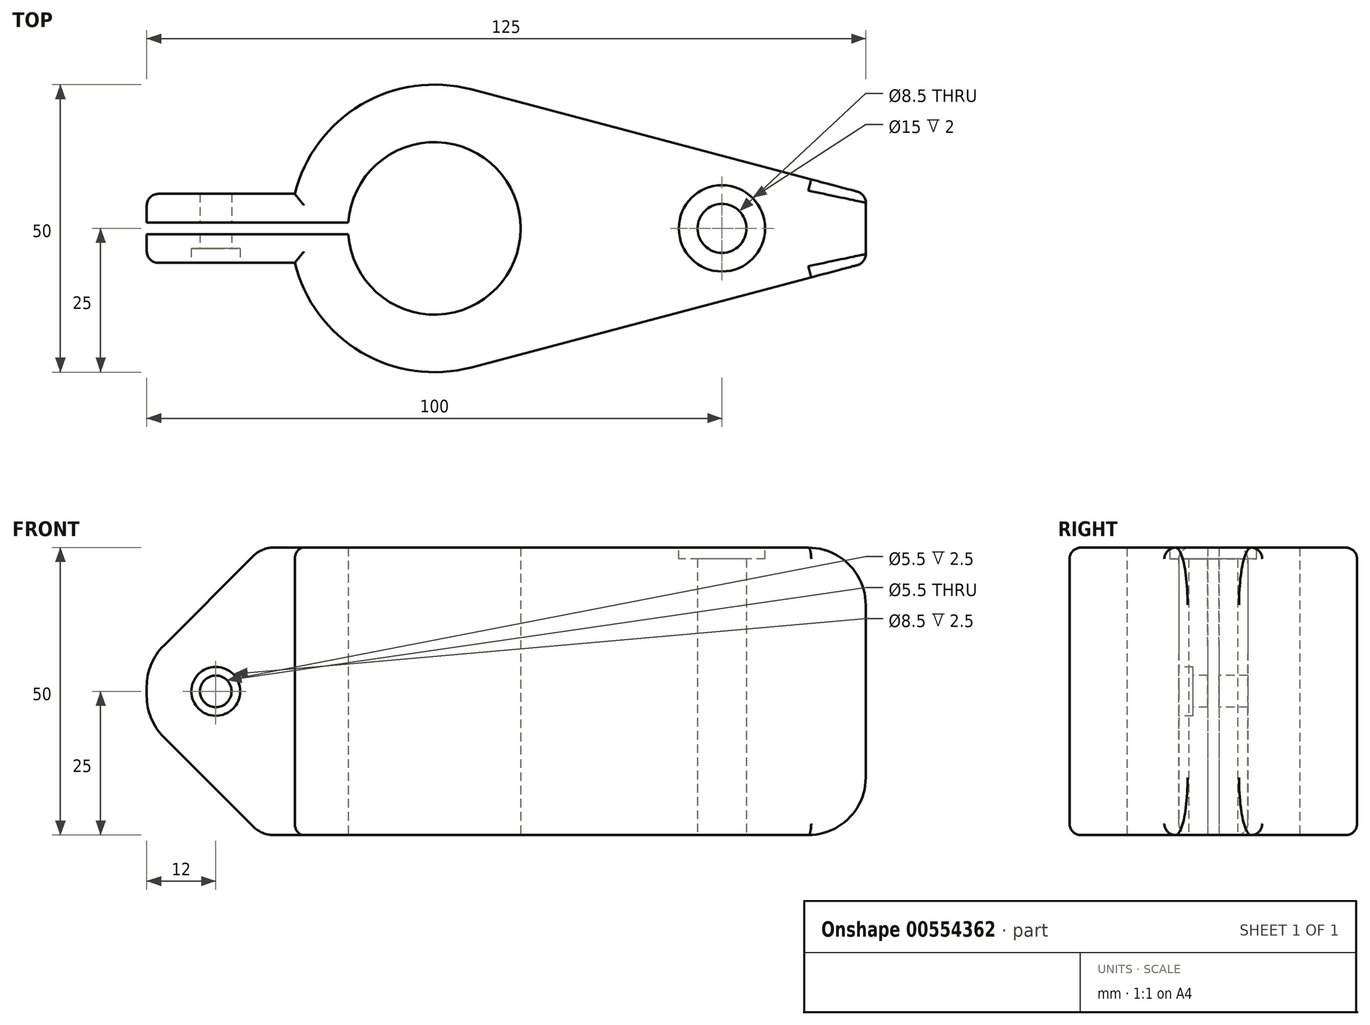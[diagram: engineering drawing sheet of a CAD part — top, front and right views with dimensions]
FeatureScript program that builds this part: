
annotation { "Feature Type Name" : "Feature", "Feature Type Description" : "" }
export const myFeature = defineFeature(function(context is Context, id is Id, definition is map)
    precondition{}
    {
        {
            var Q0;
            Q0=qCreatedBy(makeId("Top.planeOp"),FACE);
            var sketch = newSketch(context, id + "F0", { "sketchPlane" : qUnion([Q0])});
            skArc(sketch, "E0", {"start": v(-14.97, -1) * mm, "mid": v(15, 0) * mm, "end": v(-14.97, 1) * mm});
            skLineSegment(sketch, "E1", {"start": v(0, 0) * mm, "end": v(50, 0) * mm});
            skCircle(sketch, "E2", {"center": v(50, 0) * mm, "radius": 4.25 * mm});
            skLineSegment(sketch, "E3", {"start": v(75, 6) * mm, "end": v(75, 6) * mm});
            skLineSegment(sketch, "E4", {"start": v(75, -6) * mm, "end": v(75, -6) * mm});
            skLineSegment(sketch, "E5", {"start": v(0, 0) * mm, "end": v(75, 0) * mm, "construction": true});
            skLineSegment(sketch, "E6", {"start": v(75, 0) * mm, "end": v(75, 6) * mm, "construction": true});
            skLineSegment(sketch, "E7", {"start": v(75, 6) * mm, "end": v(75, 0) * mm});
            skLineSegment(sketch, "E8", {"start": v(75, -6) * mm, "end": v(75, 0) * mm});
            skArc(sketch, "E9", {"start": v(6.4, 24.17) * mm, "mid": v(-12.74, 21.5) * mm, "end": v(-24.27, 6) * mm});
            skLineSegment(sketch, "E10", {"start": v(75, 6) * mm, "end": v(6.4, 24.17) * mm});
            skLineSegment(sketch, "E11", {"start": v(75, -6) * mm, "end": v(6.4, -24.17) * mm});
            skLineSegment(sketch, "E12", {"start": v(0, 0) * mm, "end": v(0, 1) * mm});
            skLineSegment(sketch, "E13", {"start": v(-14.97, 1) * mm, "end": v(-50, 1) * mm});
            skLineSegment(sketch, "E14.bottom", {"start": v(-50, 6) * mm, "end": v(-24.27, 6) * mm});
            skLineSegment(sketch, "E14.top", {"start": v(-50, -6) * mm, "end": v(-24.27, -6) * mm});
            skLineSegment(sketch, "E15", {"start": v(0, 0) * mm, "end": v(-50, 0) * mm, "construction": true});
            skLineSegment(sketch, "E16", {"start": v(-50, 1) * mm, "end": v(-50, 6) * mm});
            skLineSegment(sketch, "E17", {"start": v(-50, -1) * mm, "end": v(-50, -6) * mm});
            skLineSegment(sketch, "E18", {"start": v(-14.97, -1) * mm, "end": v(-50, -1) * mm});
            skLineSegment(sketch, "E19", {"start": v(0, -1) * mm, "end": v(0, 0) * mm});
            skArc(sketch, "E20.trimOffspring", {"start": v(-24.27, -6) * mm, "mid": v(-12.74, -21.5) * mm, "end": v(6.4, -24.17) * mm});
            skSolve(sketch);
        }
        {
            var Q0;
            Q0=qSketchRegion(id+"F0",true);
            extrude(context, id + "F1", {"entities" : qUnion([Q0]), "depth" : 50 * mm, "offsetDistance" : 25 * mm});
        }
        {
            var Q0;
            Q0=makeQuery(id+"F1.opExtrude","CAP_FACE",FACE,{"disambiguationData":[OSD([sQuery(id+"F0.wireOp",EDGE,"E0"),sQuery(id+"F0.wireOp",EDGE,"E2"),sQuery(id+"F0.wireOp",EDGE,"E3"),sQuery(id+"F0.wireOp",EDGE,"E4"),sQuery(id+"F0.wireOp",EDGE,"E7"),sQuery(id+"F0.wireOp",EDGE,"E8"),sQuery(id+"F0.wireOp",EDGE,"E9"),sQuery(id+"F0.wireOp",EDGE,"E10"),sQuery(id+"F0.wireOp",EDGE,"E11")])],"isStart":false});
            var sketch = newSketch(context, id + "F2", { "sketchPlane" : qUnion([Q0])});
            skCircle(sketch, "E21", {"center": v(50, 0) * mm, "radius": 7.5 * mm});
            skSolve(sketch);
        }
        {
            var Q0;
            Q0=qSketchRegion(id+"F2",true);
            extrude(context, id + "F3", {"entities" : qUnion([Q0]), "operationType" : NewBodyOperationType.REMOVE, "oppositeDirection" : true, "depth" : 2 * mm, "offsetDistance" : 25 * mm});
        }
        {
            var Q0;
            Q0=makeQuery(id+"F1.opExtrude","CAP_EDGE",EDGE,{"disambiguationData":[OSD([sQuery(id+"F0.wireOp",EDGE,"E7"),sQuery(id+"F0.wireOp",EDGE,"E8")])],"isStart":false});
            var Q1;
            Q1=makeQuery(id+"F1.opExtrude","CAP_EDGE",EDGE,{"disambiguationData":[OSD([sQuery(id+"F0.wireOp",EDGE,"E7"),sQuery(id+"F0.wireOp",EDGE,"E8")])],"isStart":true});
            fillet(context, id + "F4", {"entities" : qUnion([Q0, Q1]), "radius" : 10 * mm, "tangentPropagation" : true, "allowEdgeOverflow" : false});
        }
        {
            var Q0;
            Q0=makeQuery(id+"F1.opExtrude","CAP_EDGE",EDGE,{"disambiguationData":[OSD([sQuery(id+"F0.wireOp",EDGE,"E3")])],"isStart":false});
            var Q1;
            Q1=makeQuery(id+"F1.opExtrude","CAP_EDGE",EDGE,{"disambiguationData":[OSD([sQuery(id+"F0.wireOp",EDGE,"E4")])],"isStart":false});
            var Q2;
            Q2=makeQuery(id+"F1.opExtrude","CAP_EDGE",EDGE,{"disambiguationData":[OSD([sQuery(id+"F0.wireOp",EDGE,"E10")])],"isStart":false});
            var Q3;
            Q3=makeQuery(id+"F1.opExtrude","CAP_EDGE",EDGE,{"disambiguationData":[OSD([sQuery(id+"F0.wireOp",EDGE,"E10")])],"isStart":true});
            var Q4;
            Q4=makeQuery(id+"F1.opExtrude","CAP_EDGE",EDGE,{"disambiguationData":[OSD([sQuery(id+"F0.wireOp",EDGE,"E11")])],"isStart":false});
            fillet(context, id + "F5", {"entities" : qUnion([Q0, Q1, Q2, Q3, Q4]), "radius" : 2 * mm, "tangentPropagation" : true, "allowEdgeOverflow" : false});
        }
        {
            var Q0;
            Q0=makeQuery(id+"F1.opExtrude","CAP_EDGE",EDGE,{"disambiguationData":[OSD([sQuery(id+"F0.wireOp",EDGE,"E16")])],"isStart":false});
            var Q1;
            Q1=makeQuery(id+"F1.opExtrude","CAP_EDGE",EDGE,{"disambiguationData":[OSD([sQuery(id+"F0.wireOp",EDGE,"E17")])],"isStart":false});
            var Q2;
            Q2=makeQuery(id+"F1.opExtrude","CAP_EDGE",EDGE,{"disambiguationData":[OSD([sQuery(id+"F0.wireOp",EDGE,"E17")])],"isStart":true});
            var Q3;
            Q3=makeQuery(id+"F1.opExtrude","CAP_EDGE",EDGE,{"disambiguationData":[OSD([sQuery(id+"F0.wireOp",EDGE,"E16")])],"isStart":true});
            chamfer(context, id + "F6", {"entities" : qUnion([Q0, Q1, Q2, Q3]), "width" : 20 * mm, "tangentPropagation" : true});
        }
        {
            var Q0;
            {var subQ0=sQuery(id+"F0.wireOp",EDGE,"E17");Q0=makeQuery(id+"F6.opChamfer","BLEND_EDGE",EDGE,{"blendedFrom":[makeQuery(id+"F1.opExtrude","CAP_EDGE",EDGE,{"disambiguationData":[OSD([subQ0])],"isStart":false}),makeQuery(id+"F1.opExtrude","SWEPT_FACE",FACE,{"disambiguationData":[OSD([subQ0])]})],"blendedInto":[makeQuery(id+"F1.opExtrude","SWEPT_FACE",FACE,{"disambiguationData":[OSD([subQ0])]})]});}
            var Q1;
            {var subQ0=sQuery(id+"F0.wireOp",EDGE,"E16");Q1=makeQuery(id+"F6.opChamfer","BLEND_EDGE",EDGE,{"blendedFrom":[makeQuery(id+"F1.opExtrude","CAP_EDGE",EDGE,{"disambiguationData":[OSD([subQ0])],"isStart":false}),makeQuery(id+"F1.opExtrude","SWEPT_FACE",FACE,{"disambiguationData":[OSD([subQ0])]})],"blendedInto":[makeQuery(id+"F1.opExtrude","SWEPT_FACE",FACE,{"disambiguationData":[OSD([subQ0])]})]});}
            var Q2;
            {var subQ0=sQuery(id+"F0.wireOp",EDGE,"E16");Q2=makeQuery(id+"F6.opChamfer","BLEND_EDGE",EDGE,{"blendedFrom":[makeQuery(id+"F1.opExtrude","CAP_EDGE",EDGE,{"disambiguationData":[OSD([subQ0])],"isStart":true}),makeQuery(id+"F1.opExtrude","SWEPT_FACE",FACE,{"disambiguationData":[OSD([subQ0])]})],"blendedInto":[makeQuery(id+"F1.opExtrude","SWEPT_FACE",FACE,{"disambiguationData":[OSD([subQ0])]})]});}
            var Q3;
            {var subQ0=sQuery(id+"F0.wireOp",EDGE,"E17");Q3=makeQuery(id+"F6.opChamfer","BLEND_EDGE",EDGE,{"blendedFrom":[makeQuery(id+"F1.opExtrude","CAP_EDGE",EDGE,{"disambiguationData":[OSD([subQ0])],"isStart":true}),makeQuery(id+"F1.opExtrude","SWEPT_FACE",FACE,{"disambiguationData":[OSD([subQ0])]})],"blendedInto":[makeQuery(id+"F1.opExtrude","SWEPT_FACE",FACE,{"disambiguationData":[OSD([subQ0])]})]});}
            fillet(context, id + "F7", {"entities" : qUnion([Q0, Q1, Q2, Q3]), "radius" : 10 * mm, "tangentPropagation" : true, "allowEdgeOverflow" : false});
        }
        {
            var Q0;
            {var subQ0=sQuery(id+"F0.wireOp",EDGE,"E17");Q0=makeQuery(id+"F6.opChamfer","BLEND_EDGE",EDGE,{"blendedFrom":[makeQuery(id+"F1.opExtrude","CAP_EDGE",EDGE,{"disambiguationData":[OSD([subQ0])],"isStart":false}),makeQuery(id+"F1.opExtrude","CAP_FACE",FACE,{"disambiguationData":[OSD([sQuery(id+"F0.wireOp",EDGE,"E0"),sQuery(id+"F0.wireOp",EDGE,"E2"),sQuery(id+"F0.wireOp",EDGE,"E7"),sQuery(id+"F0.wireOp",EDGE,"E8"),sQuery(id+"F0.wireOp",EDGE,"E9"),sQuery(id+"F0.wireOp",EDGE,"E10"),sQuery(id+"F0.wireOp",EDGE,"E11"),sQuery(id+"F0.wireOp",EDGE,"E13"),sQuery(id+"F0.wireOp",EDGE,"E14.bottom"),sQuery(id+"F0.wireOp",EDGE,"E14.top"),sQuery(id+"F0.wireOp",EDGE,"E16"),subQ0,sQuery(id+"F0.wireOp",EDGE,"E18"),sQuery(id+"F0.wireOp",EDGE,"E20.trimOffspring")])],"isStart":false})],"blendedInto":[makeQuery(id+"F1.opExtrude","CAP_FACE",FACE,{"disambiguationData":[OSD([sQuery(id+"F0.wireOp",EDGE,"E0"),sQuery(id+"F0.wireOp",EDGE,"E2"),sQuery(id+"F0.wireOp",EDGE,"E7"),sQuery(id+"F0.wireOp",EDGE,"E8"),sQuery(id+"F0.wireOp",EDGE,"E9"),sQuery(id+"F0.wireOp",EDGE,"E10"),sQuery(id+"F0.wireOp",EDGE,"E11"),sQuery(id+"F0.wireOp",EDGE,"E13"),sQuery(id+"F0.wireOp",EDGE,"E14.bottom"),sQuery(id+"F0.wireOp",EDGE,"E14.top"),sQuery(id+"F0.wireOp",EDGE,"E16"),subQ0,sQuery(id+"F0.wireOp",EDGE,"E18"),sQuery(id+"F0.wireOp",EDGE,"E20.trimOffspring")])],"isStart":false})]});}
            var Q1;
            {var subQ0=sQuery(id+"F0.wireOp",EDGE,"E16");Q1=makeQuery(id+"F6.opChamfer","BLEND_EDGE",EDGE,{"blendedFrom":[makeQuery(id+"F1.opExtrude","CAP_EDGE",EDGE,{"disambiguationData":[OSD([subQ0])],"isStart":false}),makeQuery(id+"F1.opExtrude","CAP_FACE",FACE,{"disambiguationData":[OSD([sQuery(id+"F0.wireOp",EDGE,"E0"),sQuery(id+"F0.wireOp",EDGE,"E2"),sQuery(id+"F0.wireOp",EDGE,"E7"),sQuery(id+"F0.wireOp",EDGE,"E8"),sQuery(id+"F0.wireOp",EDGE,"E9"),sQuery(id+"F0.wireOp",EDGE,"E10"),sQuery(id+"F0.wireOp",EDGE,"E11"),sQuery(id+"F0.wireOp",EDGE,"E13"),sQuery(id+"F0.wireOp",EDGE,"E14.bottom"),sQuery(id+"F0.wireOp",EDGE,"E14.top"),subQ0,sQuery(id+"F0.wireOp",EDGE,"E17"),sQuery(id+"F0.wireOp",EDGE,"E18"),sQuery(id+"F0.wireOp",EDGE,"E20.trimOffspring")])],"isStart":false})],"blendedInto":[makeQuery(id+"F1.opExtrude","CAP_FACE",FACE,{"disambiguationData":[OSD([sQuery(id+"F0.wireOp",EDGE,"E0"),sQuery(id+"F0.wireOp",EDGE,"E2"),sQuery(id+"F0.wireOp",EDGE,"E7"),sQuery(id+"F0.wireOp",EDGE,"E8"),sQuery(id+"F0.wireOp",EDGE,"E9"),sQuery(id+"F0.wireOp",EDGE,"E10"),sQuery(id+"F0.wireOp",EDGE,"E11"),sQuery(id+"F0.wireOp",EDGE,"E13"),sQuery(id+"F0.wireOp",EDGE,"E14.bottom"),sQuery(id+"F0.wireOp",EDGE,"E14.top"),subQ0,sQuery(id+"F0.wireOp",EDGE,"E17"),sQuery(id+"F0.wireOp",EDGE,"E18"),sQuery(id+"F0.wireOp",EDGE,"E20.trimOffspring")])],"isStart":false})]});}
            var Q2;
            {var subQ0=sQuery(id+"F0.wireOp",EDGE,"E17");Q2=makeQuery(id+"F6.opChamfer","BLEND_EDGE",EDGE,{"blendedFrom":[makeQuery(id+"F1.opExtrude","CAP_EDGE",EDGE,{"disambiguationData":[OSD([subQ0])],"isStart":true}),makeQuery(id+"F1.opExtrude","CAP_FACE",FACE,{"disambiguationData":[OSD([sQuery(id+"F0.wireOp",EDGE,"E0"),sQuery(id+"F0.wireOp",EDGE,"E2"),sQuery(id+"F0.wireOp",EDGE,"E7"),sQuery(id+"F0.wireOp",EDGE,"E8"),sQuery(id+"F0.wireOp",EDGE,"E9"),sQuery(id+"F0.wireOp",EDGE,"E10"),sQuery(id+"F0.wireOp",EDGE,"E11"),sQuery(id+"F0.wireOp",EDGE,"E13"),sQuery(id+"F0.wireOp",EDGE,"E14.bottom"),sQuery(id+"F0.wireOp",EDGE,"E14.top"),sQuery(id+"F0.wireOp",EDGE,"E16"),subQ0,sQuery(id+"F0.wireOp",EDGE,"E18"),sQuery(id+"F0.wireOp",EDGE,"E20.trimOffspring")])],"isStart":true})],"blendedInto":[makeQuery(id+"F1.opExtrude","CAP_FACE",FACE,{"disambiguationData":[OSD([sQuery(id+"F0.wireOp",EDGE,"E0"),sQuery(id+"F0.wireOp",EDGE,"E2"),sQuery(id+"F0.wireOp",EDGE,"E7"),sQuery(id+"F0.wireOp",EDGE,"E8"),sQuery(id+"F0.wireOp",EDGE,"E9"),sQuery(id+"F0.wireOp",EDGE,"E10"),sQuery(id+"F0.wireOp",EDGE,"E11"),sQuery(id+"F0.wireOp",EDGE,"E13"),sQuery(id+"F0.wireOp",EDGE,"E14.bottom"),sQuery(id+"F0.wireOp",EDGE,"E14.top"),sQuery(id+"F0.wireOp",EDGE,"E16"),subQ0,sQuery(id+"F0.wireOp",EDGE,"E18"),sQuery(id+"F0.wireOp",EDGE,"E20.trimOffspring")])],"isStart":true})]});}
            var Q3;
            {var subQ0=sQuery(id+"F0.wireOp",EDGE,"E16");Q3=makeQuery(id+"F6.opChamfer","BLEND_EDGE",EDGE,{"blendedFrom":[makeQuery(id+"F1.opExtrude","CAP_EDGE",EDGE,{"disambiguationData":[OSD([subQ0])],"isStart":true}),makeQuery(id+"F1.opExtrude","CAP_FACE",FACE,{"disambiguationData":[OSD([sQuery(id+"F0.wireOp",EDGE,"E0"),sQuery(id+"F0.wireOp",EDGE,"E2"),sQuery(id+"F0.wireOp",EDGE,"E7"),sQuery(id+"F0.wireOp",EDGE,"E8"),sQuery(id+"F0.wireOp",EDGE,"E9"),sQuery(id+"F0.wireOp",EDGE,"E10"),sQuery(id+"F0.wireOp",EDGE,"E11"),sQuery(id+"F0.wireOp",EDGE,"E13"),sQuery(id+"F0.wireOp",EDGE,"E14.bottom"),sQuery(id+"F0.wireOp",EDGE,"E14.top"),subQ0,sQuery(id+"F0.wireOp",EDGE,"E17"),sQuery(id+"F0.wireOp",EDGE,"E18"),sQuery(id+"F0.wireOp",EDGE,"E20.trimOffspring")])],"isStart":true})],"blendedInto":[makeQuery(id+"F1.opExtrude","CAP_FACE",FACE,{"disambiguationData":[OSD([sQuery(id+"F0.wireOp",EDGE,"E0"),sQuery(id+"F0.wireOp",EDGE,"E2"),sQuery(id+"F0.wireOp",EDGE,"E7"),sQuery(id+"F0.wireOp",EDGE,"E8"),sQuery(id+"F0.wireOp",EDGE,"E9"),sQuery(id+"F0.wireOp",EDGE,"E10"),sQuery(id+"F0.wireOp",EDGE,"E11"),sQuery(id+"F0.wireOp",EDGE,"E13"),sQuery(id+"F0.wireOp",EDGE,"E14.bottom"),sQuery(id+"F0.wireOp",EDGE,"E14.top"),subQ0,sQuery(id+"F0.wireOp",EDGE,"E17"),sQuery(id+"F0.wireOp",EDGE,"E18"),sQuery(id+"F0.wireOp",EDGE,"E20.trimOffspring")])],"isStart":true})]});}
            fillet(context, id + "F8", {"entities" : qUnion([Q0, Q1, Q2, Q3]), "radius" : 5 * mm, "tangentPropagation" : true, "allowEdgeOverflow" : false});
        }
        {
            var Q0;
            Q0=makeQuery(id+"F6.opChamfer","BLEND_EDGE",EDGE,{"blendedFrom":[makeQuery(id+"F1.opExtrude","CAP_EDGE",EDGE,{"disambiguationData":[OSD([sQuery(id+"F0.wireOp",EDGE,"E17")])],"isStart":false}),makeQuery(id+"F1.opExtrude","SWEPT_FACE",FACE,{"disambiguationData":[OSD([sQuery(id+"F0.wireOp",EDGE,"E14.top")])]})],"blendedInto":[makeQuery(id+"F1.opExtrude","SWEPT_FACE",FACE,{"disambiguationData":[OSD([sQuery(id+"F0.wireOp",EDGE,"E14.top")])]})]});
            var Q1;
            Q1=makeQuery(id+"F6.opChamfer","BLEND_EDGE",EDGE,{"blendedFrom":[makeQuery(id+"F1.opExtrude","CAP_EDGE",EDGE,{"disambiguationData":[OSD([sQuery(id+"F0.wireOp",EDGE,"E16")])],"isStart":false}),makeQuery(id+"F1.opExtrude","SWEPT_FACE",FACE,{"disambiguationData":[OSD([sQuery(id+"F0.wireOp",EDGE,"E14.bottom")])]})],"blendedInto":[makeQuery(id+"F1.opExtrude","SWEPT_FACE",FACE,{"disambiguationData":[OSD([sQuery(id+"F0.wireOp",EDGE,"E14.bottom")])]})]});
            fillet(context, id + "F9", {"entities" : qUnion([Q0, Q1]), "radius" : 2 * mm, "tangentPropagation" : true, "allowEdgeOverflow" : false});
        }
        {
            var Q0;
            Q0=makeQuery(id+"F1.opExtrude","SWEPT_FACE",FACE,{"disambiguationData":[OSD([sQuery(id+"F0.wireOp",EDGE,"E14.top")])]});
            var sketch = newSketch(context, id + "F10", { "sketchPlane" : qUnion([Q0])});
            skCircle(sketch, "E22", {"center": v(-38, 25) * mm, "radius": 2.75 * mm});
            skPoint(sketch, "E22.centerSnap0", {"position": v(-48, 25) * mm});
            skLineSegment(sketch, "E23", {"start": v(-48, 25) * mm, "end": v(-38, 25) * mm, "construction": true});
            skSolve(sketch);
        }
        {
            var Q0;
            Q0 = qSketchRegion(id + "F10", true);
            extrude(context, id + "F11", {"entities" : qUnion([Q0]), "operationType" : NewBodyOperationType.REMOVE, "oppositeDirection" : true, "depth" : 25 * mm, "offsetDistance" : 25 * mm});
        }
        {
            var Q0;
            Q0=makeQuery(id+"F1.opExtrude","SWEPT_FACE",FACE,{"disambiguationData":[OSD([sQuery(id+"F0.wireOp",EDGE,"E14.top")])]});
            var sketch = newSketch(context, id + "F12", { "sketchPlane" : qUnion([Q0])});
            skCircle(sketch, "E24", {"center": v(-38, 25) * mm, "radius": 4.25 * mm});
            skSolve(sketch);
        }
        {
            var Q0;
            Q0 = qSketchRegion(id + "F12", true);
            extrude(context, id + "F13", {"entities" : qUnion([Q0]), "operationType" : NewBodyOperationType.REMOVE, "oppositeDirection" : true, "depth" : 2.5 * mm, "offsetDistance" : 25 * mm});
        }
    });
